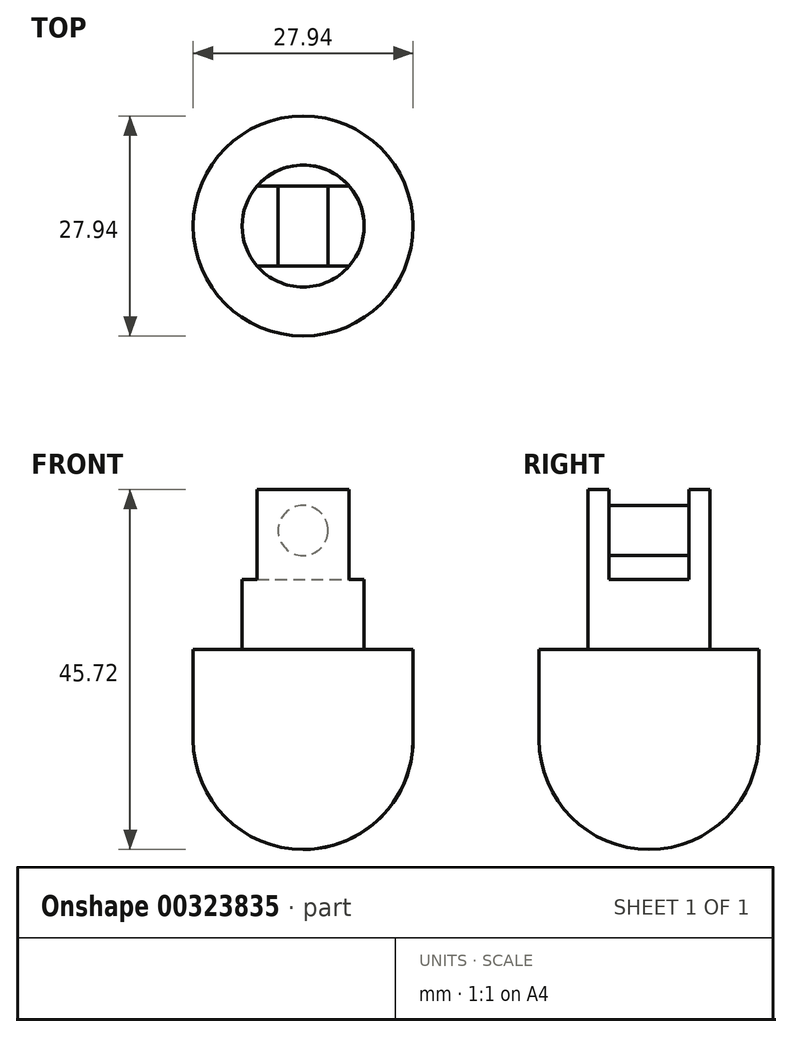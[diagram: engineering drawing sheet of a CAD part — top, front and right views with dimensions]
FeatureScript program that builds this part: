
annotation { "Feature Type Name" : "Feature", "Feature Type Description" : "" }
export const myFeature = defineFeature(function(context is Context, id is Id, definition is map)
    precondition{}
    {
        {
            var Q0;
            Q0=qCreatedBy(makeId("Top.planeOp"),FACE);
            var sketch = newSketch(context, id + "F0", { "sketchPlane" : qUnion([Q0])});
            skCircle(sketch, "E0", {"center": v(0, 0) * mm, "radius": 13.97 * mm});
            skCircle(sketch, "E1", {"center": v(0, 0) * mm, "radius": 7.75 * mm});
            skSolve(sketch);
        }
        {
            var Q0;
            Q0=makeQuery(id+"F0.imprint","IMPRINT",FACE,{"disambiguationData":[TD([[makeQuery(id+"F0.imprint","IMPRINT",EDGE,{"derivedFrom":sQuery(id+"F0.wireOp",EDGE,"E1")}),1.0]])]});
            extrude(context, id + "F1", {"entities" : qUnion([Q0]), "depth" : 20.32 * mm});
        }
        {
            var Q0;
            Q0=makeQuery(id+"F0.imprint","IMPRINT",FACE,{"disambiguationData":[TD([[makeQuery(id+"F0.imprint","IMPRINT",EDGE,{"derivedFrom":sQuery(id+"F0.wireOp",EDGE,"E0")}),1.0]])]});
            var Q1;
            Q1=makeQuery(id+"F0.imprint","IMPRINT",FACE,{"disambiguationData":[TD([[makeQuery(id+"F0.imprint","IMPRINT",EDGE,{"derivedFrom":sQuery(id+"F0.wireOp",EDGE,"E1")}),1.0]])]});
            extrude(context, id + "F2", {"entities" : qUnion([Q0, Q1]), "operationType" : NewBodyOperationType.ADD, "oppositeDirection" : true, "depth" : 25.4 * mm});
        }
        {
            var Q0;
            Q0=makeQuery(id+"F2.opExtrude","CAP_EDGE",EDGE,{"disambiguationData":[OSD([sQuery(id+"F0.wireOp",EDGE,"E0")])],"isStart":false});
            fillet(context, id + "F3", {"entities" : qUnion([Q0]), "radius" : 13.97 * mm, "tangentPropagation" : true, "allowEdgeOverflow" : false});
        }
        {
            var Q0;
            Q0=makeQuery(id+"F1.opExtrude","CAP_FACE",FACE,{"disambiguationData":[OSD([sQuery(id+"F0.wireOp",EDGE,"E1")])],"isStart":false});
            var sketch = newSketch(context, id + "F4", { "sketchPlane" : qUnion([Q0])});
            skLineSegment(sketch, "E2.bottom", {"start": v(-9.63, 5.08) * mm, "end": v(10.11, 5.08) * mm});
            skLineSegment(sketch, "E2.top", {"start": v(-9.63, -5.08) * mm, "end": v(10.11, -5.08) * mm});
            skLineSegment(sketch, "E2.left", {"start": v(-9.63, 5.08) * mm, "end": v(-9.63, -5.08) * mm});
            skLineSegment(sketch, "E2.right", {"start": v(10.11, 5.08) * mm, "end": v(10.11, -5.08) * mm});
            skCircle(sketch, "E3.0", {"center": v(0, 0) * mm, "radius": 7.75 * mm});
            skLineSegment(sketch, "E4", {"start": v(-9.63, 0) * mm, "end": v(10.11, 0) * mm, "construction": true});
            skSolve(sketch);
        }
        {
            var Q0;
            {var subQ0=sQuery(id+"F4.wireOp",EDGE,"E2.right");Q0=makeQuery(id+"F4.imprint","IMPRINT",FACE,{"disambiguationData":[TD([[makeQuery(id+"F4.imprint","IMPRINT",EDGE,{"derivedFrom":subQ0}),-1.0]])]});}
            var Q1;
            {var subQ0=sQuery(id+"F4.wireOp",EDGE,"E3.0");var subQ1=sQuery(id+"F4.wireOp",EDGE,"E2.bottom");var subQ2=makeQuery(id+"F4.imprint","INTERSECT",VERTEX,{"disambiguationData":[OD(0.0)],"derivedFrom":[subQ1,subQ0]});Q1=makeQuery(id+"F4.imprint","IMPRINT",FACE,{"disambiguationData":[TD([[makeQuery(id+"F4.imprint","IMPRINT",EDGE,{"disambiguationData":[TD([[subQ2,-1.0]])],"derivedFrom":subQ1}),-1.0]])]});}
            var Q2;
            {var subQ0=sQuery(id+"F4.wireOp",EDGE,"E2.left");Q2=makeQuery(id+"F4.imprint","IMPRINT",FACE,{"disambiguationData":[TD([[makeQuery(id+"F4.imprint","IMPRINT",EDGE,{"derivedFrom":subQ0}),1.0]])]});}
            extrude(context, id + "F5", {"entities" : qUnion([Q0, Q1, Q2]), "operationType" : NewBodyOperationType.REMOVE, "oppositeDirection" : true, "depth" : 11.43 * mm});
        }
        {
            var Q0;
            Q0=qCreatedBy(makeId("Front.planeOp"),FACE);
            var sketch = newSketch(context, id + "F6", { "sketchPlane" : qUnion([Q0])});
            skLineSegment(sketch, "E5", {"start": v(-7.75, 0) * mm, "end": v(-7.75, 8.9) * mm});
            skLineSegment(sketch, "E6", {"start": v(7.75, 8.9) * mm, "end": v(7.75, 0) * mm});
            skLineSegment(sketch, "E7.0", {"start": v(-5.85, 20.32) * mm, "end": v(5.85, 20.32) * mm});
            skCircle(sketch, "E8", {"center": v(0, 15.12) * mm, "radius": 3.18 * mm});
            skPoint(sketch, "E8.centerSnap0", {"position": v(0, 20.32) * mm});
            skSolve(sketch);
        }
        {
            var Q0;
            Q0=makeQuery(id+"F6.imprint","IMPRINT",FACE,{"disambiguationData":[TD([[makeQuery(id+"F6.imprint","IMPRINT",EDGE,{"derivedFrom":sQuery(id+"F6.wireOp",EDGE,"E8")}),1.0]])]});
            extrude(context, id + "F7", {"entities" : qUnion([Q0]), "operationType" : NewBodyOperationType.ADD, "endBound" : BoundingType.SYMMETRIC, "depth" : 12.7 * mm});
        }
    });
